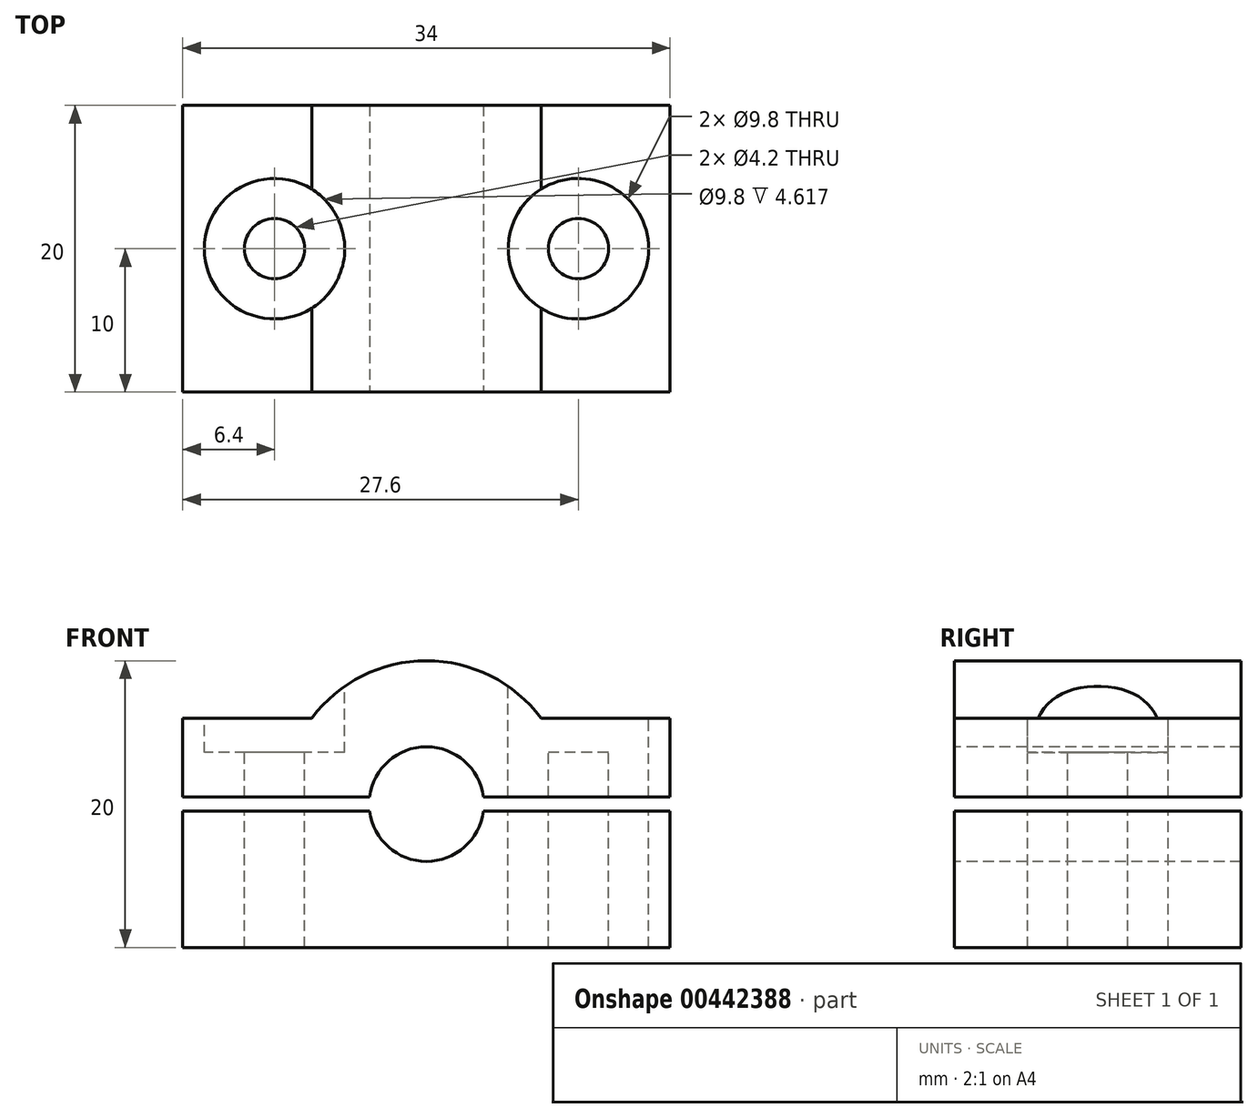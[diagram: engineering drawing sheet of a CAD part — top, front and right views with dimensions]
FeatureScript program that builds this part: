
annotation { "Feature Type Name" : "Feature", "Feature Type Description" : "" }
export const myFeature = defineFeature(function(context is Context, id is Id, definition is map)
    precondition{}
    {
        {
            var Q0;
            Q0=qCreatedBy(makeId("Top.planeOp"),FACE);
            var sketch = newSketch(context, id + "F0", { "sketchPlane" : qUnion([Q0])});
            skLineSegment(sketch, "E0.bottom", {"start": v(17, -10) * mm, "end": v(-17, -10) * mm});
            skLineSegment(sketch, "E0.top", {"start": v(17, 10) * mm, "end": v(-17, 10) * mm});
            skLineSegment(sketch, "E0.left", {"start": v(17, -10) * mm, "end": v(17, 10) * mm});
            skLineSegment(sketch, "E0.right", {"start": v(-17, -10) * mm, "end": v(-17, 10) * mm});
            skPoint(sketch, "E0.middle", {"position": v(0, 0) * mm});
            skSolve(sketch);
        }
        {
            var Q0;
            Q0 = qSketchRegion(id + "F0", true);
            extrude(context, id + "F1", {"entities" : qUnion([Q0]), "depth" : 20 * mm, "offsetDistance" : 25 * mm});
        }
        {
            var Q0;
            Q0=makeQuery(id+"F1.opExtrude","SWEPT_FACE",FACE,{"disambiguationData":[OSD([sQuery(id+"F0.wireOp",EDGE,"E0.bottom")])]});
            var sketch = newSketch(context, id + "F2", { "sketchPlane" : qUnion([Q0])});
            skCircle(sketch, "E1", {"center": v(0, 10) * mm, "radius": 4 * mm});
            skSolve(sketch);
        }
        {
            var Q0;
            Q0 = qSketchRegion(id + "F2", true);
            var Q1;
            Q1=sQuery(id+"F2.wireOp",EDGE,"E1");
            var Q2;
            Q2=makeQuery(id+"F1.opExtrude","SWEPT_FACE",FACE,{"disambiguationData":[OSD([sQuery(id+"F0.wireOp",EDGE,"E0.top")])]});
            extrude(context, id + "F3", {"entities" : qUnion([Q0]), "operationType" : NewBodyOperationType.REMOVE, "surfaceEntities" : qUnion([Q1]), "endBound" : BoundingType.UP_TO_SURFACE, "oppositeDirection" : true, "depth" : 25 * mm, "endBoundEntityFace" : qUnion([Q2]), "offsetDistance" : 25 * mm});
        }
        {
            var Q0;
            Q0=makeQuery(id+"F1.opExtrude","CAP_FACE",FACE,{"disambiguationData":[OSD([sQuery(id+"F0.wireOp",EDGE,"E0.bottom"),sQuery(id+"F0.wireOp",EDGE,"E0.top"),sQuery(id+"F0.wireOp",EDGE,"E0.left"),sQuery(id+"F0.wireOp",EDGE,"E0.right")])],"isStart":false});
            var sketch = newSketch(context, id + "F4", { "sketchPlane" : qUnion([Q0])});
            skCircle(sketch, "E2", {"center": v(-10.6, 0) * mm, "radius": 2.1 * mm});
            skCircle(sketch, "E3.MirrorC", {"center": v(10.6, 0) * mm, "radius": 2.1 * mm});
            skCircle(sketch, "E4", {"center": v(-10.6, 0) * mm, "radius": 4.9 * mm});
            skCircle(sketch, "E5.MirrorC", {"center": v(10.6, 0) * mm, "radius": 4.9 * mm});
            skSolve(sketch);
        }
        {
            var Q0;
            Q0=makeQuery(id+"F4.imprint","IMPRINT",FACE,{"disambiguationData":[TD([[makeQuery(id+"F4.imprint","IMPRINT",EDGE,{"derivedFrom":sQuery(id+"F4.wireOp",EDGE,"E2")}),-1.0]])]});
            var Q1;
            Q1=makeQuery(id+"F4.imprint","IMPRINT",FACE,{"disambiguationData":[TD([[makeQuery(id+"F4.imprint","IMPRINT",EDGE,{"derivedFrom":sQuery(id+"F4.wireOp",EDGE,"E3.MirrorC")}),1.0]])]});
            extrude(context, id + "F5", {"entities" : qUnion([Q0, Q1]), "operationType" : NewBodyOperationType.REMOVE, "oppositeDirection" : true, "depth" : 6.4 * mm, "offsetDistance" : 25 * mm});
        }
        {
            var Q0;
            Q0=makeQuery(id+"F4.imprint","IMPRINT",FACE,{"disambiguationData":[TD([[makeQuery(id+"F4.imprint","IMPRINT",EDGE,{"derivedFrom":sQuery(id+"F4.wireOp",EDGE,"E2")}),1.0]])]});
            var Q1;
            Q1=makeQuery(id+"F4.imprint","IMPRINT",FACE,{"disambiguationData":[TD([[makeQuery(id+"F4.imprint","IMPRINT",EDGE,{"derivedFrom":sQuery(id+"F4.wireOp",EDGE,"E3.MirrorC")}),-1.0]])]});
            var Q2;
            Q2=makeQuery(id+"F1.opExtrude","CAP_FACE",FACE,{"disambiguationData":[OSD([sQuery(id+"F0.wireOp",EDGE,"E0.bottom"),sQuery(id+"F0.wireOp",EDGE,"E0.top"),sQuery(id+"F0.wireOp",EDGE,"E0.left"),sQuery(id+"F0.wireOp",EDGE,"E0.right")])],"isStart":true});
            extrude(context, id + "F6", {"entities" : qUnion([Q0, Q1]), "operationType" : NewBodyOperationType.REMOVE, "endBound" : BoundingType.UP_TO_SURFACE, "oppositeDirection" : true, "depth" : 25 * mm, "endBoundEntityFace" : qUnion([Q2]), "offsetDistance" : 25 * mm});
        }
        {
            var Q0;
            Q0=makeQuery(id+"F1.opExtrude","SWEPT_FACE",FACE,{"disambiguationData":[OSD([sQuery(id+"F0.wireOp",EDGE,"E0.bottom")])]});
            var sketch = newSketch(context, id + "F7", { "sketchPlane" : qUnion([Q0])});
            skCircle(sketch, "E6", {"center": v(0, 10) * mm, "radius": 10 * mm});
            skLineSegment(sketch, "E7.bottom", {"start": v(17, 9.5) * mm, "end": v(-17, 9.5) * mm});
            skLineSegment(sketch, "E7.top", {"start": v(17, 10.5) * mm, "end": v(-17, 10.5) * mm});
            skLineSegment(sketch, "E7.left", {"start": v(17, 9.5) * mm, "end": v(17, 10.5) * mm});
            skLineSegment(sketch, "E7.right", {"start": v(-17, 9.5) * mm, "end": v(-17, 10.5) * mm});
            skLineSegment(sketch, "E8", {"start": v(-17, 16) * mm, "end": v(-8, 16) * mm});
            skLineSegment(sketch, "E9.trimOffspring", {"start": v(8, 16) * mm, "end": v(17, 16) * mm});
            skLineSegment(sketch, "E10", {"start": v(-17, 16) * mm, "end": v(-17, 20) * mm});
            skLineSegment(sketch, "E11", {"start": v(-17, 20) * mm, "end": v(17, 20) * mm});
            skLineSegment(sketch, "E12", {"start": v(17, 20) * mm, "end": v(17, 16) * mm});
            skSolve(sketch);
        }
        {
            var Q0;
            {var subQ0=sQuery(id+"F7.wireOp",EDGE,"E8");Q0=makeQuery(id+"F7.imprint","IMPRINT",FACE,{"disambiguationData":[TD([[makeQuery(id+"F7.imprint","IMPRINT",EDGE,{"derivedFrom":subQ0}),1.0]])]});}
            var Q1;
            {var subQ0=sQuery(id+"F7.wireOp",EDGE,"E9.trimOffspring");Q1=makeQuery(id+"F7.imprint","IMPRINT",FACE,{"disambiguationData":[TD([[makeQuery(id+"F7.imprint","IMPRINT",EDGE,{"derivedFrom":subQ0}),1.0]])]});}
            var Q2;
            {var subQ0=sQuery(id+"F7.wireOp",EDGE,"E7.top");var subQ1=sQuery(id+"F7.wireOp",EDGE,"E6");var subQ2=makeQuery(id+"F7.imprint","INTERSECT",VERTEX,{"disambiguationData":[OD(0.0)],"derivedFrom":[subQ1,subQ0]});Q2=makeQuery(id+"F7.imprint","IMPRINT",FACE,{"disambiguationData":[TD([[makeQuery(id+"F7.imprint","IMPRINT",EDGE,{"disambiguationData":[TD([[subQ2,1.0]])],"derivedFrom":subQ1}),1.0]])]});}
            var Q3;
            {var subQ5=sQuery(id+"F7.wireOp",EDGE,"E7.left");Q3=makeQuery(id+"F7.imprint","IMPRINT",FACE,{"disambiguationData":[TD([[makeQuery(id+"F7.imprint","IMPRINT",EDGE,{"derivedFrom":subQ5}),-1.0]])]});}
            var Q4;
            {var subQ0=sQuery(id+"F7.wireOp",EDGE,"E7.top");var subQ1=sQuery(id+"F7.wireOp",EDGE,"E6");var subQ2=makeQuery(id+"F7.imprint","INTERSECT",VERTEX,{"disambiguationData":[OD(1.0)],"derivedFrom":[subQ1,subQ0]});Q4=makeQuery(id+"F7.imprint","IMPRINT",FACE,{"disambiguationData":[TD([[makeQuery(id+"F7.imprint","IMPRINT",EDGE,{"disambiguationData":[TD([[subQ2,-1.0]])],"derivedFrom":subQ1}),1.0]])]});}
            var Q5;
            {var subQ5=sQuery(id+"F7.wireOp",EDGE,"E7.right");Q5=makeQuery(id+"F7.imprint","IMPRINT",FACE,{"disambiguationData":[TD([[makeQuery(id+"F7.imprint","IMPRINT",EDGE,{"derivedFrom":subQ5}),1.0]])]});}
            var Q6;
            Q6=makeQuery(id+"F1.opExtrude","SWEPT_FACE",FACE,{"disambiguationData":[OSD([sQuery(id+"F0.wireOp",EDGE,"E0.top")])]});
            extrude(context, id + "F8", {"entities" : qUnion([Q0, Q1, Q2, Q3, Q4, Q5]), "operationType" : NewBodyOperationType.REMOVE, "endBound" : BoundingType.UP_TO_SURFACE, "oppositeDirection" : true, "depth" : 25 * mm, "endBoundEntityFace" : qUnion([Q6]), "offsetDistance" : 25 * mm});
        }
    });
